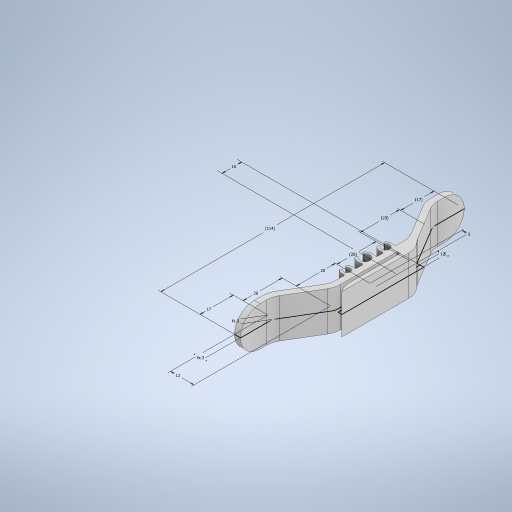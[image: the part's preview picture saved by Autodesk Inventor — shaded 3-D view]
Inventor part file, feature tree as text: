
AUTODESK INVENTOR PART (.ipt)
format: ipt  version: 2023 (Build 270158030, 158C)  size: 389,120 bytes
history: native  units: mm
features: fillet x4, sketch x2, extrude x2, other x1
ambient origin geometry x8: Origin, YZ Plane, XZ Plane, XY Plane, X Axis, Y Axis, Z Axis, Center Point
bodies: Body1 (feature_tree)
feature tree (9):
  sketch  "Sketch2"  dims[d9=3.0mm d16=3.0mm d17=3.0mm d18=17.0mm]
  extrude  "Extrusion2"  Depth=3.0mm
  fillet  "Fillet1"  Radius=3.0mm
  fillet  "Fillet2"  Radius=17.0mm
  extrude  "Extrusion3"  Depth=12.0mm
  fillet  "Fillet3"  Radius=20.0mm
  fillet  "Fillet4"  Radius=114.0mm
  other  "cable holder"
  sketch  "Sketch4"  dims[d19=20.0mm d20=12.0mm d21=20.0mm d22=114.0mm d23=20.0mm d24=20.0mm d25=17.0mm d28=20.0mm d29=0.0mm d30=2.0mm d31=1.5mm d32=10.0mm d33=10.0mm d34=10.0mm d36=10.0mm d37=10.0mm d38=7.210321mm d39=7.25mm d40=3.3mm d41=4.0mm d42=5.0mm d43=1.2mm d44=1.2mm d45=1.2mm d46=2.5mm d47=1.25mm d48=1.65mm d49=0.825mm d50=2.0mm d51=1.0mm d52=20.0mm d53=0.0mm d54=0.7mm d55=0.7mm]
